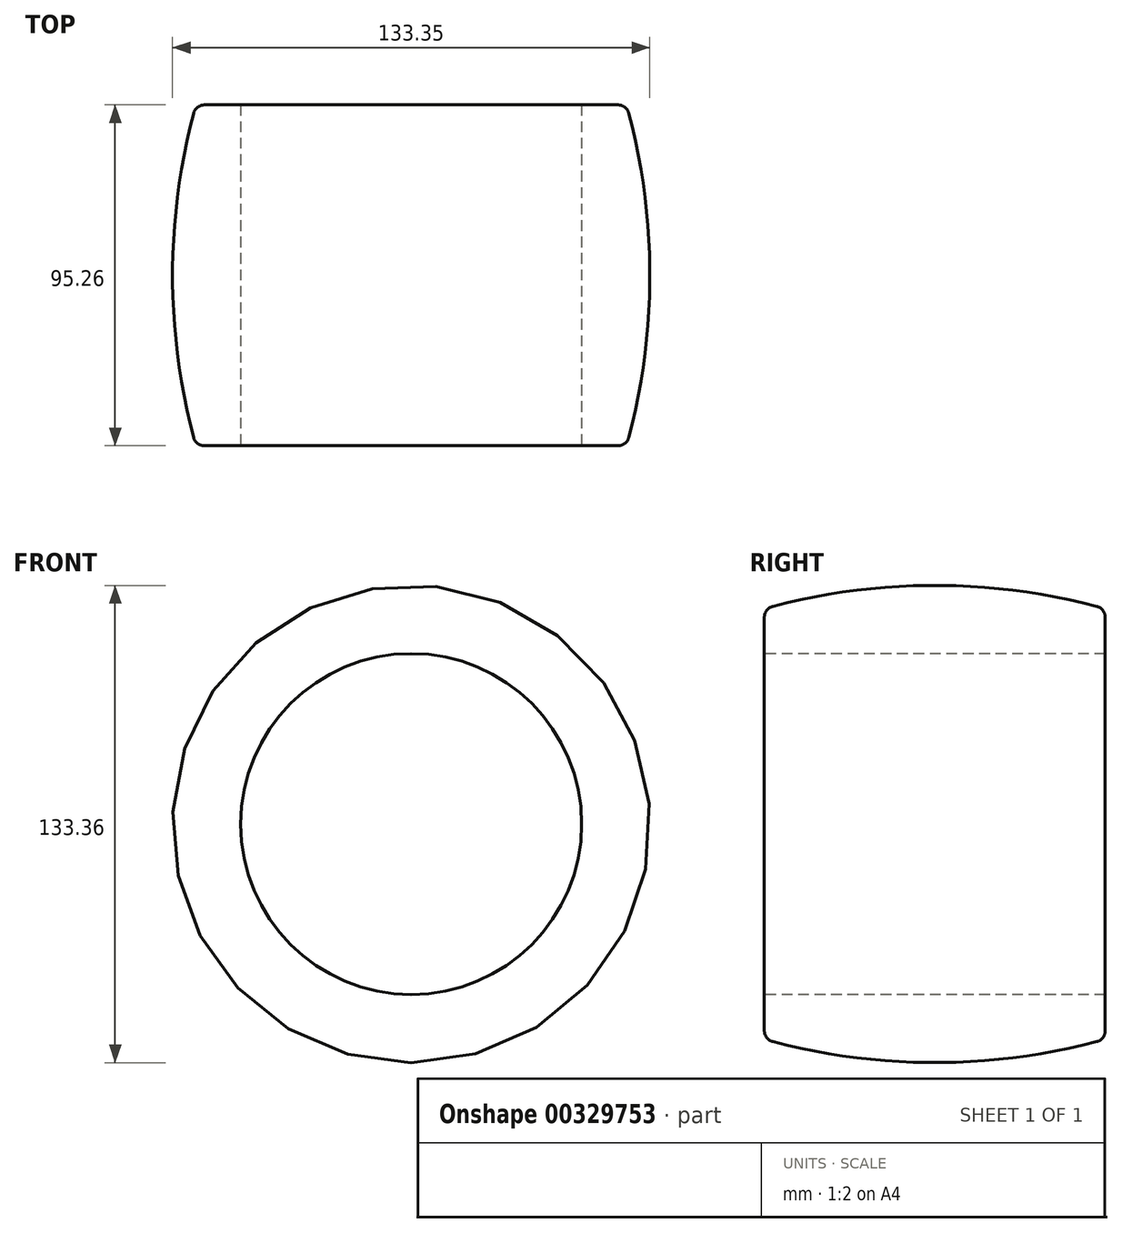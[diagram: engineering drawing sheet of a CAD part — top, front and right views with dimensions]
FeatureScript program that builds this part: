
annotation { "Feature Type Name" : "Feature", "Feature Type Description" : "" }
export const myFeature = defineFeature(function(context is Context, id is Id, definition is map)
    precondition{}
    {
        {
            var Q0;
            Q0=qCreatedBy(makeId("Top.planeOp"),FACE);
            var sketch = newSketch(context, id + "F0", { "sketchPlane" : qUnion([Q0])});
            skLineSegment(sketch, "E0.bottom", {"start": v(-7.1, 47.62) * mm, "end": v(3.03, 47.63) * mm});
            skLineSegment(sketch, "E0.top", {"start": v(-7.1, -47.63) * mm, "end": v(3.03, -47.63) * mm});
            skPoint(sketch, "E0.middle", {"position": v(0, 0) * mm});
            skArc(sketch, "E1", {"start": v(-10.17, 45.26) * mm, "mid": v(-16.02, 0) * mm, "end": v(-10.17, -45.26) * mm});
            skLineSegment(sketch, "E2.right", {"start": v(15.73, 41.28) * mm, "end": v(15.73, -41.27) * mm});
            skLineSegment(sketch, "E3.bottom", {"start": v(15.73, -1.48) * mm, "end": v(50.65, -1.48) * mm});
            skLineSegment(sketch, "E3.right", {"start": v(50.65, -1.48) * mm, "end": v(50.65, 0) * mm});
            skLineSegment(sketch, "E4", {"start": v(15.73, 0) * mm, "end": v(15.73, -1.48) * mm});
            skLineSegment(sketch, "E5.trimOffspring", {"start": v(15.73, 0) * mm, "end": v(50.65, 0) * mm});
            skPoint(sketch, "E6.visualSharp", {"position": v(-9.53, 47.62) * mm});
            skArc(sketch, "E6.filletArc", {"start": v(-7.1, 47.63) * mm, "mid": v(-9.03, 46.96) * mm, "end": v(-10.17, 45.26) * mm});
            skPoint(sketch, "E7.visualSharp", {"position": v(-9.52, -47.63) * mm});
            skArc(sketch, "E7.filletArc", {"start": v(-10.17, -45.26) * mm, "mid": v(-9.03, -46.96) * mm, "end": v(-7.1, -47.63) * mm});
            skLineSegment(sketch, "E8", {"start": v(3.03, 47.63) * mm, "end": v(3.03, -47.63) * mm});
            skLineSegment(sketch, "E9", {"start": v(3.03, 47.63) * mm, "end": v(3.03, 41.28) * mm});
            skLineSegment(sketch, "E10", {"start": v(3.03, 41.28) * mm, "end": v(15.73, 41.28) * mm});
            skLineSegment(sketch, "E11", {"start": v(15.73, -41.27) * mm, "end": v(3.03, -41.27) * mm});
            skSolve(sketch);
        }
        {
            var Q0;
            Q0=makeQuery(id+"F0.imprint","IMPRINT",FACE,{"disambiguationData":[TD([[makeQuery(id+"F0.imprint","IMPRINT",EDGE,{"derivedFrom":sQuery(id+"F0.wireOp",EDGE,"E0.bottom")}),-1.0]])]});
            var Q1;
            {var subQ3=sQuery(id+"F0.wireOp",EDGE,"E4");Q1=makeQuery(id+"F0.imprint","IMPRINT",FACE,{"disambiguationData":[TD([[makeQuery(id+"F0.imprint","IMPRINT",EDGE,{"derivedFrom":subQ3}),-1.0]])]});}
            var Q2;
            Q2=sQuery(id+"F0.wireOp",EDGE,"E3.right");
            revolve(context, id + "F1", {"entities" : qUnion([Q0, Q1]), "axis" : qUnion([Q2]), "revolveType" : RevolveType.FULL});
        }
    });
